# Revit family: 596e3fb7-9965-4cb7-93ce-71489160c183
name_source: partatom
category: Electrical Fixtures
revit_build: Autodesk Revit 2016 (Build: 20161004_0715(x64)
units: mm (PartAtom-declared; Revit-internal decimal feet)

## family parameters
Cut with Voids When Loaded = No
Host = Face
Maintain Annotation Orientation = No
OmniClass Number = 23.75.35.17.17.11
OmniClass Title = Ceiling Fans
Part Type = Normal
Room Calculation Point = No
Round Connector Dimension = Use Diameter
Shared = No

## types (1)
- See Type Catalog
    Airfoil Finishes = Caramel or Cocoa or Polished Aluminum
    Airfoil Material = Wood - Big Ass Fan - Birch - Solid Stained Dark Polished
    Amps Maximum = Bamboo: 0.24 A, Aluminum: 0.24 A
    Amps Minimum = Bamboo: 0.39 A, Aluminum: 0.39 A
    Apparent Load = 0 VA
    Controller = Haiku Home app; handheld remote supplied
    Default Elevation = 0"
    Description = Haiku H Series 60In Dia
    Environment = For indoor use only
    Extension Tube For Universal Mount = 7"
    Fan Configuration = Please Confirm Configuration With Cut Sheet
    Fan Diameter = 52In
    Fan Height = 12 77/256"
    Fan Height With Light = 12 205/256"
    Fan Height Without Light = 12 77/256"
    Hanging Weight = Bamboo: 14 lb, Aluminum: 16.5 lb
    Hardware = Metal - Big Ass Fan - Oil-Rubbed - Bronze
    IP rating = X2
    Low and Standard Mount = Yes
    Manufacturer = Big Ass Fans
    Model = H Series Bamboo Low Profile Mount
    Model Number = S3127-S0-XX-XX-02-C-01
    Motor And Assembly Finishes = Caramel: white, black, satin nickel, oil-rubbed bronze, Cocoa: black, satin nickel, oil-rubbed bronze,Aluminum:Black or White
    Motor Type = EC motor with digital inverter drive
    Motor Warranty For Commercial = 2 years in the US and Canada
    Motor Warranty For Residential = Limited lifetime in the US and Canada
    Mounting Type = 1
    Nominal Fan Height = 12 141/256"
    Nominal Tube Length = 8 115/128"
    Number Of Airfoils = 3
    Number Of Fan Speeds = 7
    Operating Frequency = 200–240 VAC, 1 Phase, 50/60 Hz
    Operating Voltage = 100–125 VAC, 1 Phase, 50/60 Hz
    Operational Temperature Range = 32 to 104° F (0 to 40° C)
    Optional Light Kit = 16 dimmable light settings
    Other Components Warranty For Commercial = 1 year in the US and Canada
    Other Components Warranty For Residential = 1 year in the US and Canada
    Power Connector = Power Connection
    Power Factor = 1
    RPM Maximum = Bamboo: 178 RPM, Aluminum: 178 RPM
    RPM Minimum = Bamboo: 49 RPM, Aluminum: 49 RPM
    Revit Object Download Link = http://library.smartbim.com
    Sound Level At Max Speed = < 35 dBA
    Type Image = <None>
    URL = http://www.bigassfans.com
    Universal Mount = No
    Voltage = 0 V
    Watts Maximum = Bamboo: 14.81 W, Aluminum: 14.81 W
    Watts Minimum = Bamboo: 1.49 W, Aluminum: 2.21 W

## geometry (parser evidence)
native form markers: Blend x2, Sweep x15
no freeform markers — native parametric forms only
